# Revit family: Strittekasse_VHQ_12-15_p_i_t_40110015
name_source: partatom
category: Generic Models
units: mm (PartAtom-declared; Revit-internal decimal feet)

## family parameters
Always vertical = No
Can host rebar = No
Cut with Voids When Loaded = No
Part Type = Normal
Room Calculation Point = No
Round Connector Dimension = Use Diameter
Shared = No
Work Plane-Based = Yes

## types (3) — shared parameters
Array Count = 8
CenterToCenter = 150 mm
Default Elevation = 1219 mm
Distance From Start = 100 mm  [stored 0.328084 ft]
Metal = Metal Panel
Rebar = Rebar, BSt 500 S
Rebar Top Height = 170 mm  [stored 0.557743 ft]
Sheet Metal Length = 1250 mm  [stored 4.10105 ft]
Technical Data Sheet = https://haucon.dk
Website Link = https://haucon.dk

## per-type parameters (varying)
| type | Rebar Bottom Height | Rebar Ø | Sheet Metal Height | Sheet Metal Width |
| VHQ 8/15 | 320 mm  [stored 1.04987 ft] | 8 mm  [stored 0.0262467 ft] | 30 mm  [stored 0.0984252 ft] | 50 mm  [stored 0.164042 ft] |
| VHQ 10/15 | 390 mm  [stored 1.27953 ft] | 10 mm  [stored 0.0328084 ft] | 30 mm  [stored 0.0984252 ft] | 50 mm  [stored 0.164042 ft] |
| VHQ 12/15 | 460 mm  [stored 1.50919 ft] | 12 mm  [stored 0.0393701 ft] | 40 mm  [stored 0.131234 ft] | 80 mm  [stored 0.262467 ft] |

note: [stored X ft] marks values corroborated as IEEE doubles in the binary element streams (Revit-internal decimal feet)

## geometry (parser evidence)
native form markers: Sweep x5
no freeform markers — native parametric forms only
